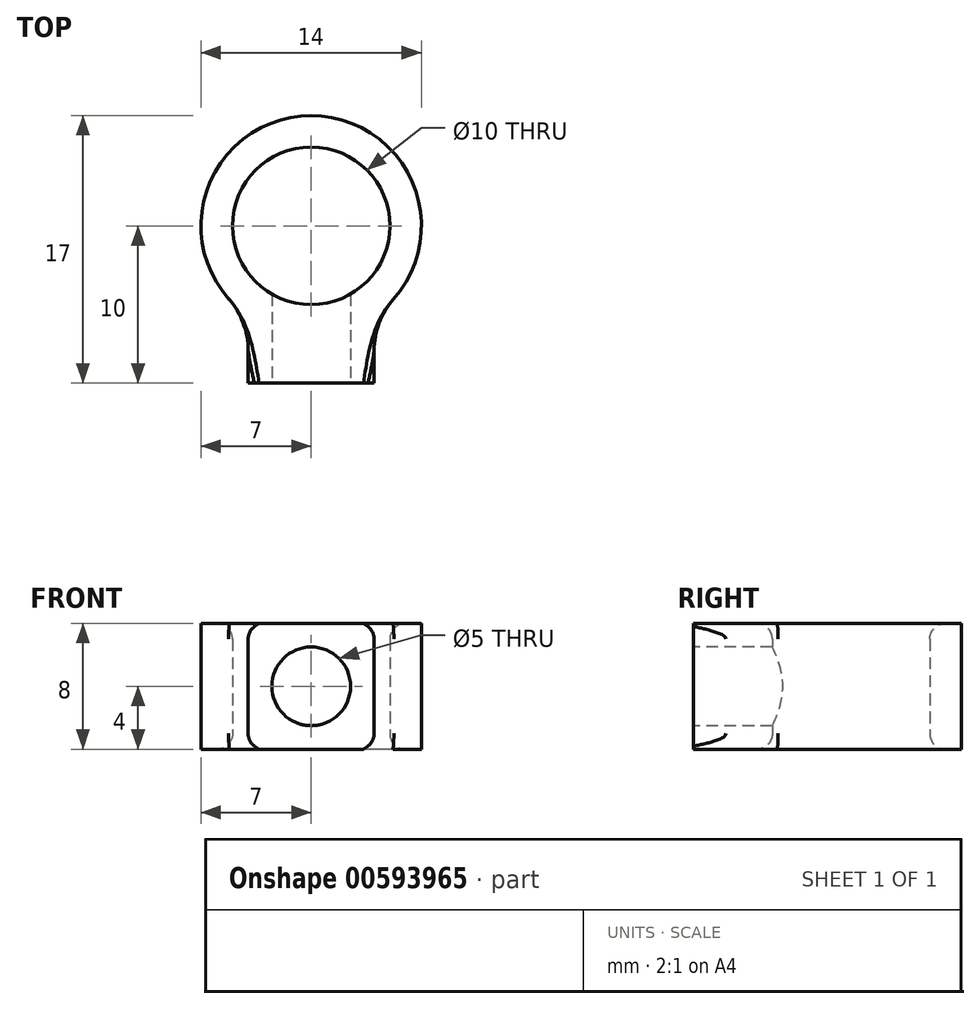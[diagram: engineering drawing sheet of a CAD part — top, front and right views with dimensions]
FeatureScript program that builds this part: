
annotation { "Feature Type Name" : "Feature", "Feature Type Description" : "" }
export const myFeature = defineFeature(function(context is Context, id is Id, definition is map)
    precondition{}
    {
        {
            var Q0;
            Q0=qCreatedBy(makeId("Top.planeOp"),FACE);
            var sketch = newSketch(context, id + "F0", { "sketchPlane" : qUnion([Q0])});
            skCircle(sketch, "E0", {"center": v(0, 0) * mm, "radius": 5 * mm});
            skCircle(sketch, "E1", {"center": v(0, 0) * mm, "radius": 7 * mm});
            skLineSegment(sketch, "E2.bottom", {"start": v(-4, 0) * mm, "end": v(4, 0) * mm});
            skLineSegment(sketch, "E2.top", {"start": v(-4, -10) * mm, "end": v(4, -10) * mm});
            skLineSegment(sketch, "E2.left", {"start": v(-4, 0) * mm, "end": v(-4, -10) * mm});
            skLineSegment(sketch, "E2.right", {"start": v(4, 0) * mm, "end": v(4, -10) * mm});
            skSolve(sketch);
        }
        {
            var Q0;
            {var subQ0=sQuery(id+"F0.wireOp",EDGE,"E2.left");var subQ1=sQuery(id+"F0.wireOp",EDGE,"E0");var subQ2=makeQuery(id+"F0.imprint","INTERSECT",VERTEX,{"derivedFrom":[subQ1,subQ0]});Q0=makeQuery(id+"F0.imprint","IMPRINT",FACE,{"disambiguationData":[TD([[makeQuery(id+"F0.imprint","IMPRINT",EDGE,{"disambiguationData":[TD([[subQ2,1.0]])],"derivedFrom":subQ1}),-1.0]])]});}
            var Q1;
            {var subQ0=sQuery(id+"F0.wireOp",EDGE,"E2.left");var subQ1=sQuery(id+"F0.wireOp",EDGE,"E0");var subQ2=makeQuery(id+"F0.imprint","INTERSECT",VERTEX,{"derivedFrom":[subQ1,subQ0]});Q1=makeQuery(id+"F0.imprint","IMPRINT",FACE,{"disambiguationData":[TD([[makeQuery(id+"F0.imprint","IMPRINT",EDGE,{"disambiguationData":[TD([[subQ2,-1.0]])],"derivedFrom":subQ1}),-1.0]])]});}
            var Q2;
            {var subQ5=sQuery(id+"F0.wireOp",EDGE,"E2.top");Q2=makeQuery(id+"F0.imprint","IMPRINT",FACE,{"disambiguationData":[TD([[makeQuery(id+"F0.imprint","IMPRINT",EDGE,{"derivedFrom":subQ5}),1.0]])]});}
            extrude(context, id + "F1", {"entities" : qUnion([Q0, Q1, Q2]), "depth" : 8 * mm, "offsetDistance" : 25 * mm});
        }
        {
            var Q0;
            Q0=makeQuery(id+"F1.opExtrude","SWEPT_FACE",FACE,{"disambiguationData":[OSD([sQuery(id+"F0.wireOp",EDGE,"E2.top")])]});
            var sketch = newSketch(context, id + "F2", { "sketchPlane" : qUnion([Q0])});
            skPoint(sketch, "E3", {"position": v(4, 4) * mm});
            skPoint(sketch, "E4", {"position": v(-4, 4) * mm});
            skPoint(sketch, "E5", {"position": v(0, 4) * mm});
            skPoint(sketch, "E5.positionSnap0", {"position": v(0, 8) * mm});
            skSolve(sketch);
        }
        {
            var Q0;
            Q0=sQuery(id+"F2.wireOp",VERTEX,"E5");
            var Q1;
            Q1=makeQuery(id+"F1.opExtrude","SWEPT_BODY",BODY,{"disambiguationData":[OSD([sQuery(id+"F0.wireOp",EDGE,"E0"),sQuery(id+"F0.wireOp",EDGE,"E1"),sQuery(id+"F0.wireOp",EDGE,"E2.top"),sQuery(id+"F0.wireOp",EDGE,"E2.left"),sQuery(id+"F0.wireOp",EDGE,"E2.right")])]});
            hole(context, id + "F3", {"style" : HoleStyle.SIMPLE, "endStyle" : HoleEndStyle.BLIND, "holeDiameter" : 5 * mm, "majorDiameter" : 5 * mm, "holeDepth" : 10 * mm, "isTappedThrough" : true, "tappedDepth" : 12 * mm, "tapClearance" : 3, "locations" : qUnion([Q0]), "scope" : qUnion([Q1])});
        }
        {
            var Q0;
            Q0=makeQuery(id+"F1.opExtrude","CAP_EDGE",EDGE,{"disambiguationData":[OSD([sQuery(id+"F0.wireOp",EDGE,"E0")])],"isStart":false});
            var Q1;
            Q1=makeQuery(id+"F1.opExtrude","CAP_EDGE",EDGE,{"disambiguationData":[OSD([sQuery(id+"F0.wireOp",EDGE,"E0")])],"isStart":true});
            fillet(context, id + "F4", {"entities" : qUnion([Q0, Q1]), "radius" : 1 * mm, "tangentPropagation" : true, "allowEdgeOverflow" : false});
        }
        {
            var Q0;
            Q0=makeQuery(id+"F1.opExtrude","CAP_EDGE",EDGE,{"disambiguationData":[OSD([sQuery(id+"F0.wireOp",EDGE,"E2.right")])],"isStart":true});
            var Q1;
            Q1=makeQuery(id+"F1.opExtrude","CAP_EDGE",EDGE,{"disambiguationData":[OSD([sQuery(id+"F0.wireOp",EDGE,"E2.left")])],"isStart":true});
            var Q2;
            Q2=makeQuery(id+"F1.opExtrude","CAP_EDGE",EDGE,{"disambiguationData":[OSD([sQuery(id+"F0.wireOp",EDGE,"E2.left")])],"isStart":false});
            var Q3;
            Q3=makeQuery(id+"F1.opExtrude","CAP_EDGE",EDGE,{"disambiguationData":[OSD([sQuery(id+"F0.wireOp",EDGE,"E2.right")])],"isStart":false});
            fillet(context, id + "F5", {"entities" : qUnion([Q0, Q1, Q2, Q3]), "radius" : 1 * mm, "tangentPropagation" : true, "allowEdgeOverflow" : false});
        }
        {
            var Q0;
            Q0=makeQuery(id+"F1.opExtrude","SWEPT_EDGE",EDGE,{"disambiguationData":[OSD([sQuery(id+"F0.wireOp",EDGE,"E1"),sQuery(id+"F0.wireOp",EDGE,"E2.left")])]});
            var Q1;
            Q1=makeQuery(id+"F1.opExtrude","SWEPT_EDGE",EDGE,{"disambiguationData":[OSD([sQuery(id+"F0.wireOp",EDGE,"E1"),sQuery(id+"F0.wireOp",EDGE,"E2.right")])]});
            fillet(context, id + "F6", {"entities" : qUnion([Q0, Q1]), "radius" : 5 * mm, "tangentPropagation" : true, "allowEdgeOverflow" : false});
        }
    });
